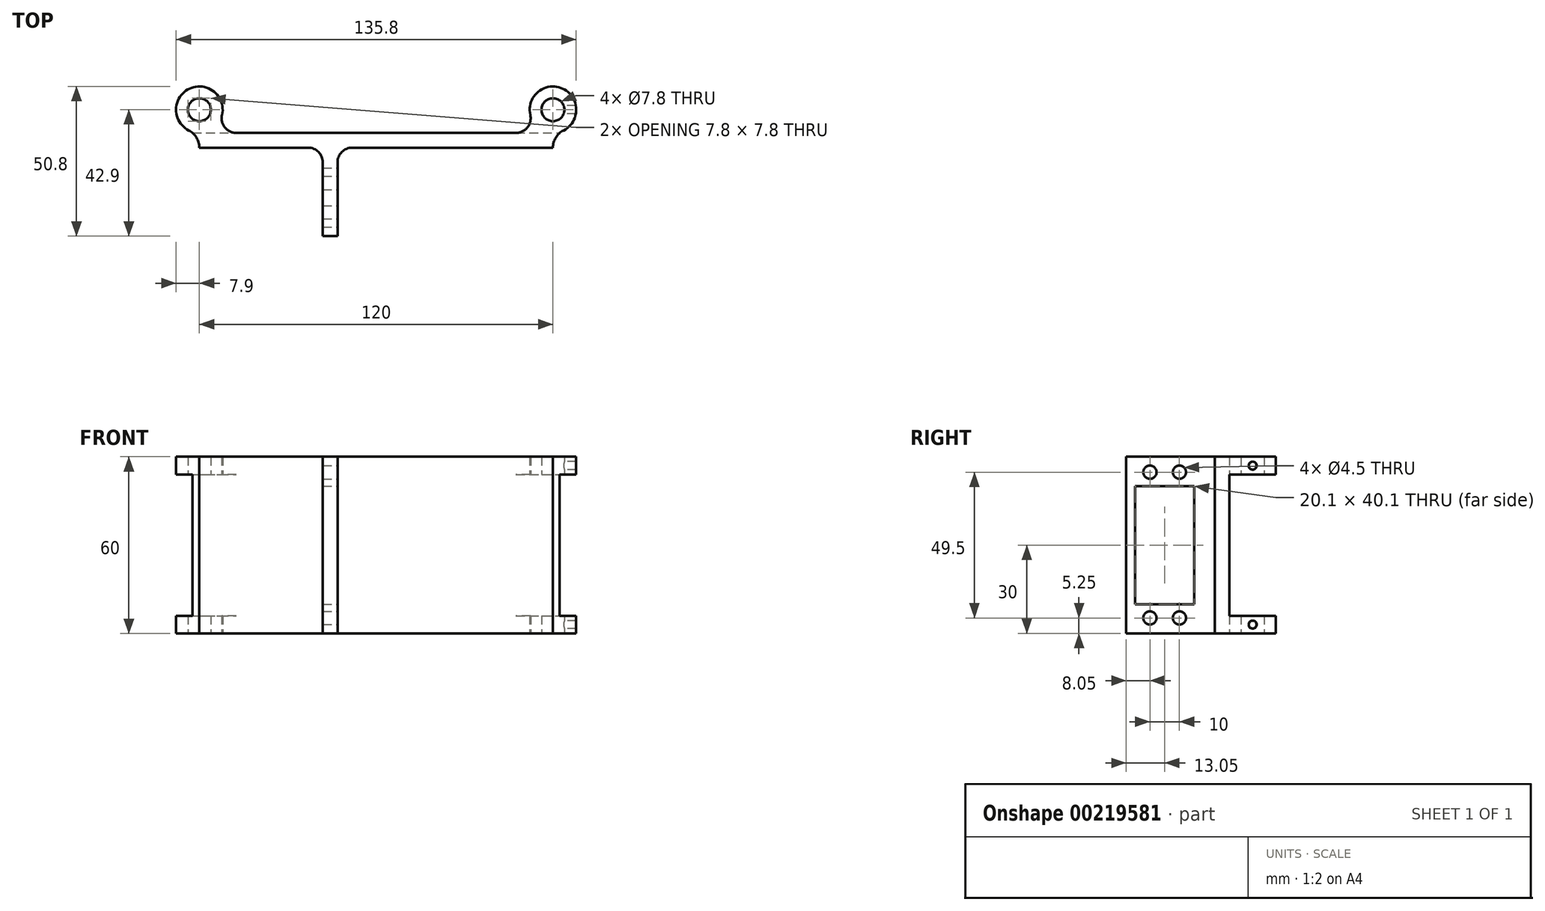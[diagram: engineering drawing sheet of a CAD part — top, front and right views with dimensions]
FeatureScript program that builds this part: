
annotation { "Feature Type Name" : "Feature", "Feature Type Description" : "" }
export const myFeature = defineFeature(function(context is Context, id is Id, definition is map)
    precondition{}
    {
        {
            var Q0;
            Q0=qCreatedBy(makeId("Top.planeOp"),FACE);
            var sketch = newSketch(context, id + "F0", { "sketchPlane" : qUnion([Q0])});
            skLineSegment(sketch, "E0.bottom", {"start": v(-60, 0) * mm, "end": v(60, 0) * mm});
            skLineSegment(sketch, "E0.top", {"start": v(-60, -5) * mm, "end": v(60, -5) * mm});
            skLineSegment(sketch, "E0.left", {"start": v(-60, 0) * mm, "end": v(-60, -5) * mm});
            skLineSegment(sketch, "E0.right", {"start": v(60, 0) * mm, "end": v(60, -5) * mm});
            skCircle(sketch, "E1", {"center": v(60, 7.9) * mm, "radius": 7.9 * mm});
            skCircle(sketch, "E2", {"center": v(-60, 7.9) * mm, "radius": 7.9 * mm});
            skCircle(sketch, "E3", {"center": v(-60, 7.9) * mm, "radius": 3.9 * mm});
            skCircle(sketch, "E4", {"center": v(60, 7.9) * mm, "radius": 3.9 * mm});
            skArc(sketch, "E5", {"start": v(-52.3, 6.12) * mm, "mid": v(-51.34, 1.89) * mm, "end": v(-47.43, 0) * mm});
            skArc(sketch, "E6", {"start": v(-60, -5) * mm, "mid": v(-60.97, -1.56) * mm, "end": v(-63.6, 0.86) * mm});
            skArc(sketch, "E7", {"start": v(47.43, 0) * mm, "mid": v(51.34, 1.89) * mm, "end": v(52.3, 6.12) * mm});
            skArc(sketch, "E8", {"start": v(63.6, 0.86) * mm, "mid": v(60.97, -1.56) * mm, "end": v(60, -5) * mm});
            skLineSegment(sketch, "E9.bottom", {"start": v(-18.1, -5) * mm, "end": v(-13.1, -5) * mm});
            skLineSegment(sketch, "E9.top", {"start": v(-18.1, -35) * mm, "end": v(-13.1, -35) * mm});
            skLineSegment(sketch, "E9.left", {"start": v(-18.1, -5) * mm, "end": v(-18.1, -35) * mm});
            skLineSegment(sketch, "E9.right", {"start": v(-13.1, -5) * mm, "end": v(-13.1, -35) * mm});
            skSolve(sketch);
        }
        {
            var Q0;
            Q0 = qSketchRegion(id + "F0", true);
            extrude(context, id + "F1", {"entities" : qUnion([Q0]), "depth" : 60 * mm});
        }
        {
            var Q0;
            Q0=makeQuery(id+"F1.opExtrude","SWEPT_FACE",FACE,{"disambiguationData":[OSD([sQuery(id+"F0.wireOp",EDGE,"E9.right")])]});
            var sketch = newSketch(context, id + "F2", { "sketchPlane" : qUnion([Q0])});
            skLineSegment(sketch, "E10.bottom", {"start": v(-32, 50.05) * mm, "end": v(-11.9, 50.05) * mm});
            skLineSegment(sketch, "E10.top", {"start": v(-32, 9.95) * mm, "end": v(-11.9, 9.95) * mm});
            skLineSegment(sketch, "E10.left", {"start": v(-32, 50.05) * mm, "end": v(-32, 9.95) * mm});
            skLineSegment(sketch, "E10.right", {"start": v(-11.9, 50.05) * mm, "end": v(-11.9, 9.95) * mm});
            skLineSegment(sketch, "E11", {"start": v(-32, 30) * mm, "end": v(-11.9, 30) * mm, "construction": true});
            skLineSegment(sketch, "E12", {"start": v(-21.95, 50.05) * mm, "end": v(-21.95, 9.95) * mm, "construction": true});
            skCircle(sketch, "E13", {"center": v(-26.95, 54.75) * mm, "radius": 2.25 * mm});
            skCircle(sketch, "E14.MirrorC", {"center": v(-16.95, 54.75) * mm, "radius": 2.25 * mm});
            skCircle(sketch, "E15.MirrorC", {"center": v(-16.95, 5.25) * mm, "radius": 2.25 * mm});
            skCircle(sketch, "E16.MirrorC", {"center": v(-26.95, 5.25) * mm, "radius": 2.25 * mm});
            skSolve(sketch);
        }
        {
            var Q0;
            Q0 = qSketchRegion(id + "F2", true);
            extrude(context, id + "F3", {"entities" : qUnion([Q0]), "operationType" : NewBodyOperationType.REMOVE, "endBound" : BoundingType.THROUGH_ALL, "oppositeDirection" : true, "depth" : 25 * mm});
        }
        {
            var Q0;
            Q0=makeQuery(id+"F1.opExtrude","CAP_FACE",FACE,{"disambiguationData":[OSD([sQuery(id+"F0.wireOp",EDGE,"E0.bottom"),sQuery(id+"F0.wireOp",EDGE,"E0.top"),sQuery(id+"F0.wireOp",EDGE,"E1"),sQuery(id+"F0.wireOp",EDGE,"E2"),sQuery(id+"F0.wireOp",EDGE,"E3"),sQuery(id+"F0.wireOp",EDGE,"E4"),sQuery(id+"F0.wireOp",EDGE,"E5"),sQuery(id+"F0.wireOp",EDGE,"E6"),sQuery(id+"F0.wireOp",EDGE,"E7"),sQuery(id+"F0.wireOp",EDGE,"E8"),sQuery(id+"F0.wireOp",EDGE,"E9.top"),sQuery(id+"F0.wireOp",EDGE,"E9.left"),sQuery(id+"F0.wireOp",EDGE,"E9.right")])],"isStart":false});
            var sketch = newSketch(context, id + "F4", { "sketchPlane" : qUnion([Q0])});
            skLineSegment(sketch, "E17.bottom", {"start": v(-79.7, -5) * mm, "end": v(82.75, -5) * mm});
            skLineSegment(sketch, "E17.top", {"start": v(-79.7, 30.92) * mm, "end": v(82.75, 30.92) * mm});
            skLineSegment(sketch, "E17.left", {"start": v(-79.7, -5) * mm, "end": v(-79.7, 30.92) * mm});
            skLineSegment(sketch, "E17.right", {"start": v(82.75, -5) * mm, "end": v(82.75, 30.92) * mm});
            skSolve(sketch);
        }
        {
            var Q0;
            Q0=qCreatedBy(makeId("Right.planeOp"),FACE);
            var sketch = newSketch(context, id + "F5", { "sketchPlane" : qUnion([Q0])});
            skLineSegment(sketch, "E18.0.1", {"start": v(0, 0) * mm, "end": v(0, 60) * mm});
            skLineSegment(sketch, "E18.0.3", {"start": v(0, 60) * mm, "end": v(0, 0) * mm});
            skLineSegment(sketch, "E19.bottom", {"start": v(0, 54) * mm, "end": v(34.22, 54) * mm});
            skLineSegment(sketch, "E19.top", {"start": v(0, 6) * mm, "end": v(34.22, 6) * mm});
            skLineSegment(sketch, "E19.left", {"start": v(0, 54) * mm, "end": v(0, 6) * mm});
            skLineSegment(sketch, "E19.right", {"start": v(34.22, 54) * mm, "end": v(34.22, 6) * mm});
            skLineSegment(sketch, "E20", {"start": v(0, 60) * mm, "end": v(0, 54) * mm, "construction": true});
            skLineSegment(sketch, "E21", {"start": v(0, 6) * mm, "end": v(0, 0) * mm, "construction": true});
            skSolve(sketch);
        }
        {
            var Q0;
            Q0 = qSketchRegion(id + "F5", true);
            extrude(context, id + "F6", {"entities" : qUnion([Q0]), "operationType" : NewBodyOperationType.REMOVE, "endBound" : BoundingType.THROUGH_ALL, "oppositeDirection" : true, "depth" : 25 * mm, "hasSecondDirection" : true, "secondDirectionBound" : SecondDirectionBoundingType.THROUGH_ALL, "secondDirectionOppositeDirection" : false, "secondDirectionDepth" : 25 * mm});
        }
        {
            var Q0;
            Q0=makeQuery(id+"F1.opExtrude","SWEPT_EDGE",EDGE,{"disambiguationData":[OSD([sQuery(id+"F0.wireOp",EDGE,"E0.top"),sQuery(id+"F0.wireOp",EDGE,"E9.bottom"),sQuery(id+"F0.wireOp",EDGE,"E9.right")])]});
            var Q1;
            Q1=makeQuery(id+"F1.opExtrude","SWEPT_EDGE",EDGE,{"disambiguationData":[OSD([sQuery(id+"F0.wireOp",EDGE,"E0.top"),sQuery(id+"F0.wireOp",EDGE,"E9.bottom"),sQuery(id+"F0.wireOp",EDGE,"E9.left")])]});
            fillet(context, id + "F7", {"entities" : qUnion([Q0, Q1]), "radius" : 5 * mm, "tangentPropagation" : true, "allowEdgeOverflow" : false});
        }
        {
            var Q0;
            Q0=qCreatedBy(makeId("Right.planeOp"),FACE);
            cPlane(context, id + "F8", {"entities" : qUnion([Q0]), "cplaneType" : CPlaneType.OFFSET, "offset" : 60 * mm, "width" : 150 * mm, "height" : 150 * mm});
        }
        {
            var Q0;
            Q0=qCreatedBy(id+"F8.planeOp",FACE);
            var sketch = newSketch(context, id + "F9", { "sketchPlane" : qUnion([Q0])});
            skLineSegment(sketch, "E22", {"start": v(4, 54) * mm, "end": v(4, 60) * mm});
            skLineSegment(sketch, "E23", {"start": v(11.8, 60) * mm, "end": v(11.8, 54) * mm});
            skLineSegment(sketch, "E24", {"start": v(4, 0) * mm, "end": v(4, 6) * mm});
            skLineSegment(sketch, "E25", {"start": v(11.8, 6) * mm, "end": v(11.8, 0) * mm});
            skLineSegment(sketch, "E26", {"start": v(11.8, 57) * mm, "end": v(4, 57) * mm, "construction": true});
            skLineSegment(sketch, "E27", {"start": v(4, 3) * mm, "end": v(11.8, 3) * mm, "construction": true});
            skCircle(sketch, "E28", {"center": v(7.9, 57) * mm, "radius": 1.35 * mm});
            skCircle(sketch, "E29", {"center": v(7.9, 3) * mm, "radius": 1.35 * mm});
            skSolve(sketch);
        }
        {
            var Q0;
            Q0 = qSketchRegion(id + "F9", true);
            extrude(context, id + "F10", {"entities" : qUnion([Q0]), "operationType" : NewBodyOperationType.REMOVE, "endBound" : BoundingType.THROUGH_ALL, "depth" : 25 * mm});
        }
    });
